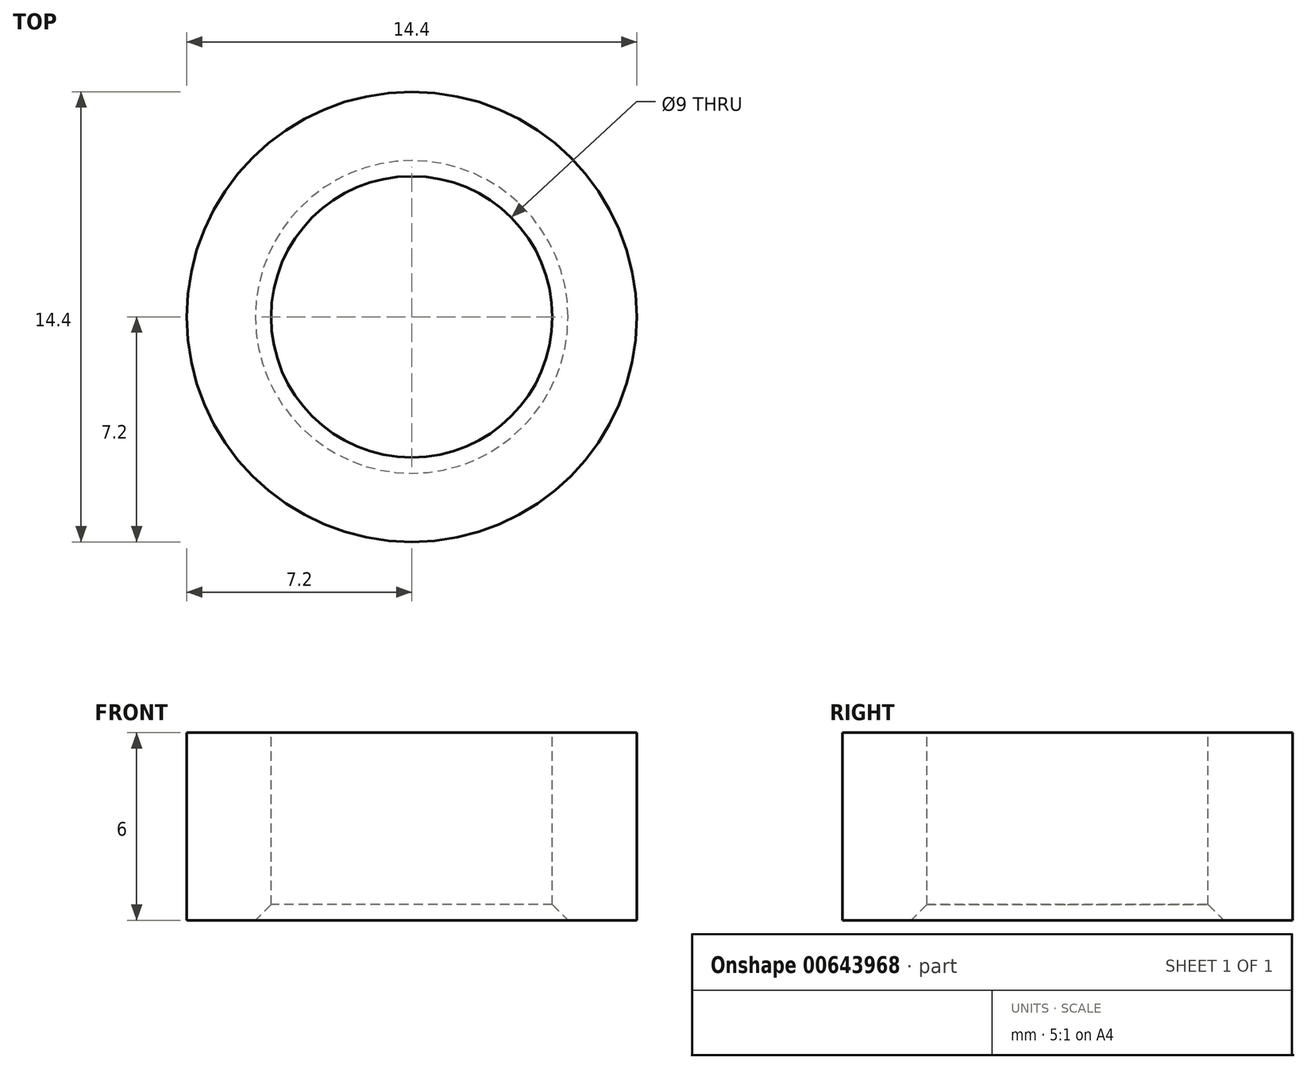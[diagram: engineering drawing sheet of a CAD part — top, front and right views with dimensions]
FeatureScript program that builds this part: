
annotation { "Feature Type Name" : "Feature", "Feature Type Description" : "" }
export const myFeature = defineFeature(function(context is Context, id is Id, definition is map)
    precondition{}
    {
        {
            var Q0;
            Q0=qCreatedBy(makeId("Top.planeOp"),FACE);
            var sketch = newSketch(context, id + "F0", { "sketchPlane" : qUnion([Q0])});
            skCircle(sketch, "E0", {"center": v(0, 0) * mm, "radius": 7.2 * mm});
            skSolve(sketch);
        }
        {
            var Q0;
            Q0=makeQuery(id+"F0.imprint","IMPRINT",FACE,{"disambiguationData":[TD([[makeQuery(id+"F0.imprint","IMPRINT",EDGE,{"derivedFrom":sQuery(id+"F0.wireOp",EDGE,"E0")}),1.0]])]});
            extrude(context, id + "F1", {"entities" : qUnion([Q0]), "depth" : 6 * mm, "offsetDistance" : 25 * mm});
        }
        {
            var Q0;
            Q0=makeQuery(id+"F1.opExtrude","CAP_FACE",FACE,{"disambiguationData":[OSD([sQuery(id+"F0.wireOp",EDGE,"E0")])],"isStart":false});
            var sketch = newSketch(context, id + "F2", { "sketchPlane" : qUnion([Q0])});
            skCircle(sketch, "E1", {"center": v(0, 0) * mm, "radius": 4.5 * mm});
            skSolve(sketch);
        }
        {
            var Q0;
            Q0=makeQuery(id+"F2.imprint","IMPRINT",FACE,{"disambiguationData":[TD([[makeQuery(id+"F2.imprint","IMPRINT",EDGE,{"derivedFrom":sQuery(id+"F2.wireOp",EDGE,"E1")}),1.0]])]});
            extrude(context, id + "F3", {"entities" : qUnion([Q0]), "operationType" : NewBodyOperationType.REMOVE, "endBound" : BoundingType.THROUGH_ALL, "oppositeDirection" : true, "depth" : 25 * mm, "offsetDistance" : 25 * mm});
        }
        {
            var Q0;
            Q0=makeQuery(id+"F3.boolean.opBoolean","COPY",EDGE,{"derivedFrom":makeQuery(id+"F3.opExtrude","CAP_EDGE",EDGE,{"disambiguationData":[OSD([sQuery(id+"F2.wireOp",EDGE,"E1")])],"isStart":true})});
            var Q1;
            Q1=makeQuery(id+"F3.boolean.opBoolean","INTERSECT",EDGE,{"derivedFrom":[makeQuery(id+"F1.opExtrude","CAP_FACE",FACE,{"disambiguationData":[OSD([sQuery(id+"F0.wireOp",EDGE,"E0")])],"isStart":true}),makeQuery(id+"F3.opExtrude","SWEPT_FACE",FACE,{"disambiguationData":[OSD([sQuery(id+"F2.wireOp",EDGE,"E1")])]})]});
            chamfer(context, id + "F4", {"entities" : qUnion([Q0, Q1]), "chamferType" : ChamferType.OFFSET_ANGLE, "width" : 0.5 * mm, "oppositeDirection" : false, "angle" : 45 * degree, "tangentPropagation" : true});
        }
    });
